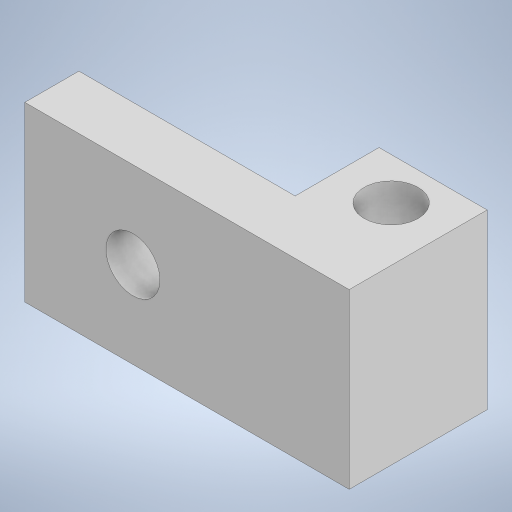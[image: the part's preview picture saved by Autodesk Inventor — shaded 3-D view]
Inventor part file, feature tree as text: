
AUTODESK INVENTOR PART (.ipt)
format: ipt  version: 2023 (Build 270158000, 158)  size: 212,480 bytes
history: native  units: in
note: dims shown in document units (in); Inventor stores cm internally (conversion verified against a paired STEP export)
features: extrude x3, sketch x3
ambient origin geometry x8: Origin, YZ Plane, XZ Plane, XY Plane, X Axis, Y Axis, Z Axis, Center Point
bodies: Solid1 (feature_tree)
feature tree (6):
  extrude  "Extrusion1"  Depth=0.6299in
  extrude  "Extrusion2"  Depth=0.3937in
  extrude  "Extrusion3"  Depth=0.1969in TaperAngle=0.0deg
  sketch  "Sketch1"  dims[d0=0.7874in d1=0.6299in]
  sketch  "Sketch2"  dims[d2=0.315in d3=0.3937in]
  sketch  "Sketch3"  dims[d4=0.1969in d5=0.1969in d6=0.0in d7=0.3937in d8=0.3055in d9=0.1969in d10=0.6299in d11=0.0in d12=0.3543in d13=0.0in]
